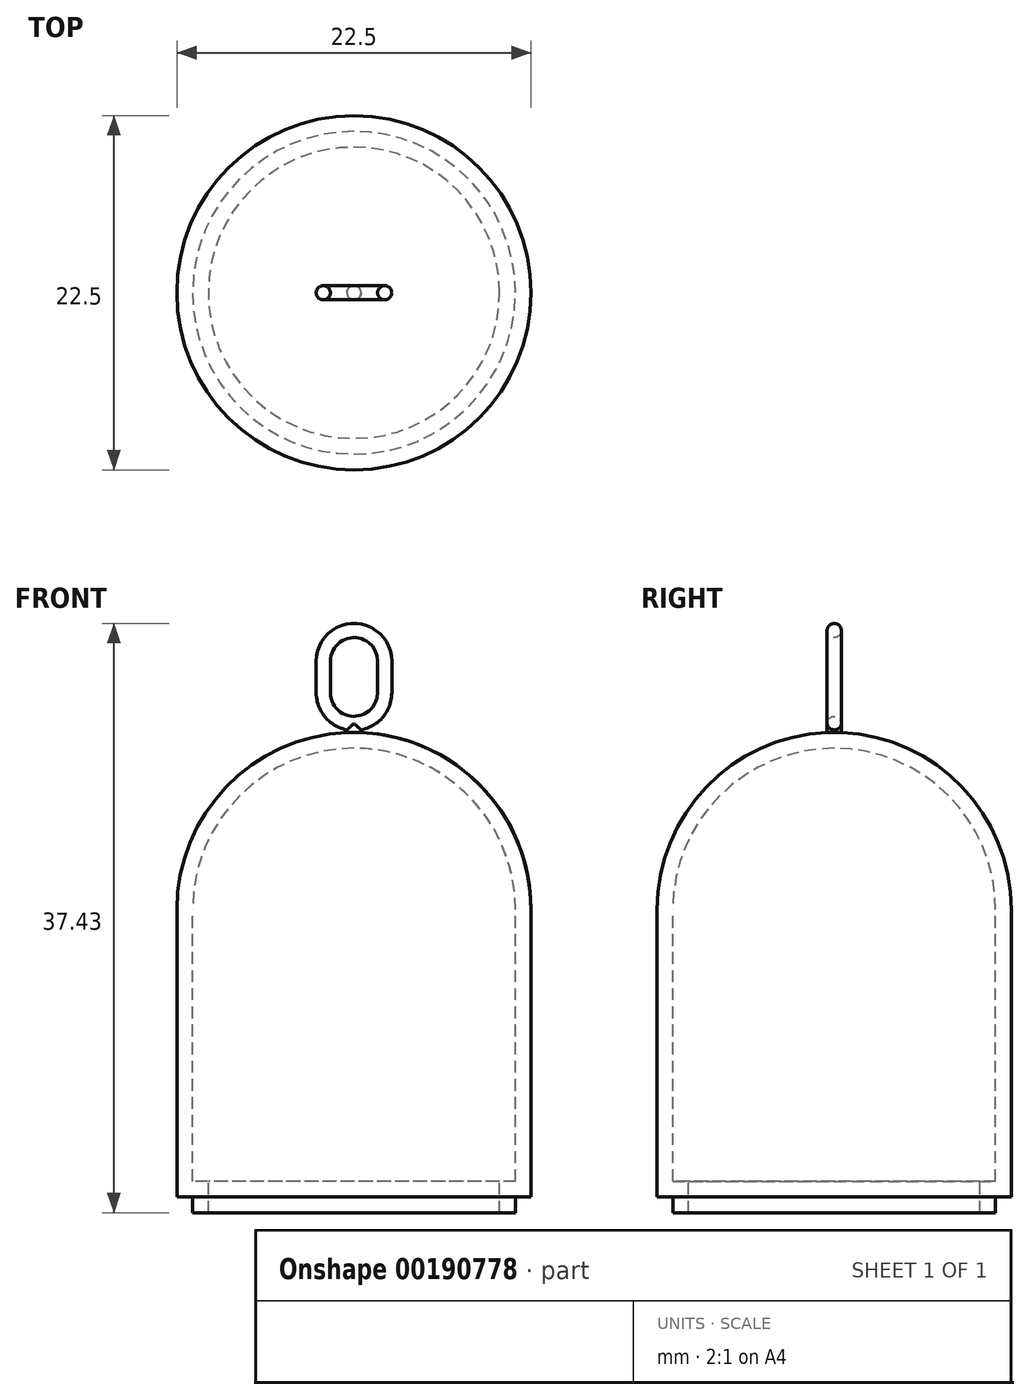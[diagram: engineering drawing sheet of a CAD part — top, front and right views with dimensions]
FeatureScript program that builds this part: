
annotation { "Feature Type Name" : "Feature", "Feature Type Description" : "" }
export const myFeature = defineFeature(function(context is Context, id is Id, definition is map)
    precondition{}
    {
        {
            var Q0;
            Q0=qCreatedBy(makeId("Front.planeOp"),FACE);
            var sketch = newSketch(context, id + "F0", { "sketchPlane" : qUnion([Q0])});
            skLineSegment(sketch, "E0.left", {"start": v(11.25, 18.75) * mm, "end": v(11.25, 0) * mm});
            skPoint(sketch, "E0.middle", {"position": v(0, 0) * mm});
            skPoint(sketch, "E1.visualSharp", {"position": v(11.25, 30) * mm});
            skArc(sketch, "E1.filletArc", {"start": v(11.25, 18.75) * mm, "mid": v(7.95, 26.7) * mm, "end": v(0, 30) * mm});
            skPoint(sketch, "E2", {"position": v(11.25, 0) * mm});
            skPoint(sketch, "E3", {"position": v(0, 30) * mm});
            skPoint(sketch, "E0.right.start.orphan", {"position": v(-11.25, 30) * mm});
            skPoint(sketch, "E0.top.end.orphan", {"position": v(-11.25, -30) * mm});
            skPoint(sketch, "E4.orphan", {"position": v(11.25, -30) * mm});
            skPoint(sketch, "E5", {"position": v(11.25, 0.5) * mm});
            skLineSegment(sketch, "E6", {"start": v(11.25, 0.5) * mm, "end": v(10.25, 0.5) * mm});
            skLineSegment(sketch, "E7", {"start": v(10.25, 0.5) * mm, "end": v(10.25, 0) * mm});
            skLineSegment(sketch, "E8", {"start": v(10.25, 0) * mm, "end": v(10.25, -0.5) * mm});
            skArc(sketch, "E9.0", {"start": v(10.25, 18.75) * mm, "mid": v(7.25, 26) * mm, "end": v(0, 29) * mm});
            skLineSegment(sketch, "E9.1", {"start": v(10.25, 18.75) * mm, "end": v(10.25, 1.5) * mm});
            skPoint(sketch, "E10", {"position": v(11.25, 1.5) * mm});
            skLineSegment(sketch, "E11", {"start": v(10.25, 1.5) * mm, "end": v(9.25, 1.5) * mm});
            skLineSegment(sketch, "E12", {"start": v(9.25, 1.5) * mm, "end": v(9.25, -0.5) * mm});
            skLineSegment(sketch, "E13", {"start": v(9.25, -0.5) * mm, "end": v(10.25, -0.5) * mm});
            skLineSegment(sketch, "E14", {"start": v(0, 30) * mm, "end": v(0, 29) * mm});
            skLineSegment(sketch, "E15.bottom", {"start": v(0, 31.03) * mm, "end": v(0, 31.03) * mm});
            skLineSegment(sketch, "E15.top", {"start": v(0, 36.03) * mm, "end": v(0, 36.03) * mm});
            skLineSegment(sketch, "E15.left", {"start": v(1.5, 32.53) * mm, "end": v(1.5, 34.53) * mm});
            skLineSegment(sketch, "E15.right", {"start": v(-1.5, 32.53) * mm, "end": v(-1.5, 34.53) * mm});
            skPoint(sketch, "E15.middle", {"position": v(0, 33.53) * mm});
            skLineSegment(sketch, "E16", {"start": v(-11.25, 30) * mm, "end": v(11.25, 30) * mm, "construction": true});
            skLineSegment(sketch, "E17", {"start": v(11.25, -30) * mm, "end": v(-11.25, -30) * mm, "construction": true});
            skLineSegment(sketch, "E18", {"start": v(-11.25, 30) * mm, "end": v(-11.25, -30) * mm, "construction": true});
            skLineSegment(sketch, "E19", {"start": v(11.25, 30) * mm, "end": v(11.25, -30) * mm, "construction": true});
            skPoint(sketch, "E20.visualSharp", {"position": v(1.5, 36.03) * mm});
            skArc(sketch, "E20.filletArc", {"start": v(1.5, 34.53) * mm, "mid": v(1.06, 35.6) * mm, "end": v(0, 36.03) * mm});
            skPoint(sketch, "E21.visualSharp", {"position": v(1.5, 31.03) * mm});
            skArc(sketch, "E21.filletArc", {"start": v(0, 31.03) * mm, "mid": v(1.06, 31.47) * mm, "end": v(1.5, 32.53) * mm});
            skPoint(sketch, "E22.visualSharp", {"position": v(-1.5, 31.03) * mm});
            skArc(sketch, "E22.filletArc", {"start": v(-1.5, 32.53) * mm, "mid": v(-1.06, 31.47) * mm, "end": v(0, 31.03) * mm});
            skPoint(sketch, "E23.visualSharp", {"position": v(-1.5, 36.03) * mm});
            skArc(sketch, "E23.filletArc", {"start": v(0, 36.03) * mm, "mid": v(-1.06, 35.6) * mm, "end": v(-1.5, 34.53) * mm});
            skLineSegment(sketch, "E24.0", {"start": v(2.4, 32.53) * mm, "end": v(2.4, 34.53) * mm});
            skArc(sketch, "E24.1", {"start": v(0, 36.93) * mm, "mid": v(-1.7, 36.23) * mm, "end": v(-2.4, 34.53) * mm});
            skLineSegment(sketch, "E24.2", {"start": v(-2.4, 32.53) * mm, "end": v(-2.4, 34.53) * mm});
            skArc(sketch, "E24.3", {"start": v(2.4, 34.53) * mm, "mid": v(1.7, 36.23) * mm, "end": v(0, 36.93) * mm});
            skArc(sketch, "E24.4", {"start": v(-2.4, 32.53) * mm, "mid": v(-1.7, 30.83) * mm, "end": v(0, 30.13) * mm});
            skArc(sketch, "E24.5", {"start": v(0, 30.13) * mm, "mid": v(1.7, 30.83) * mm, "end": v(2.4, 32.53) * mm});
            skLineSegment(sketch, "E25", {"start": v(0, 33.53) * mm, "end": v(2.4, 33.53) * mm, "construction": true});
            skLineSegment(sketch, "E26", {"start": v(0, 33.53) * mm, "end": v(-2.4, 33.53) * mm, "construction": true});
            skLineSegment(sketch, "E27.bottom", {"start": v(0.45, 30.3) * mm, "end": v(-0.45, 30.3) * mm});
            skLineSegment(sketch, "E27.top", {"start": v(0.45, 29.8) * mm, "end": v(-0.45, 29.8) * mm});
            skLineSegment(sketch, "E27.left", {"start": v(0.45, 30.3) * mm, "end": v(0.45, 29.8) * mm});
            skLineSegment(sketch, "E27.right", {"start": v(-0.45, 30.3) * mm, "end": v(-0.45, 29.8) * mm});
            skPoint(sketch, "E27.middle", {"position": v(0, 30.06) * mm});
            skLineSegment(sketch, "E28", {"start": v(10.25, 6.5) * mm, "end": v(-11.25, 6.5) * mm, "construction": true});
            skLineSegment(sketch, "E29", {"start": v(8.25, 6.5) * mm, "end": v(8.25, 3.5) * mm});
            skLineSegment(sketch, "E30", {"start": v(8.25, 3.5) * mm, "end": v(6.25, 3.5) * mm});
            skLineSegment(sketch, "E31", {"start": v(6.25, 3.5) * mm, "end": v(6.25, -0.5) * mm});
            skLineSegment(sketch, "E32", {"start": v(6.25, -0.5) * mm, "end": v(11.25, -0.5) * mm});
            skSolve(sketch);
        }
        {
            var Q0;
            Q0=qCreatedBy(makeId("Top.planeOp"),FACE);
            var sketch = newSketch(context, id + "F1", { "sketchPlane" : qUnion([Q0])});
            skCircle(sketch, "E33", {"center": v(0, 0) * mm, "radius": 11.25 * mm});
            skSolve(sketch);
        }
        {
            var Q0;
            {var subQ0=sQuery(id+"F0.wireOp",EDGE,"E14");var subQ1=sQuery(id+"F0.wireOp",EDGE,"E1.filletArc");var subQ2=makeQuery(id+"F0.imprint","INTERSECT",VERTEX,{"derivedFrom":[subQ1,subQ0]});Q0=makeQuery(id+"F0.imprint","IMPRINT",FACE,{"disambiguationData":[TD([[makeQuery(id+"F0.imprint","IMPRINT",EDGE,{"disambiguationData":[TD([[subQ2,1.0]])],"derivedFrom":subQ1}),1.0]])]});}
            var Q1;
            {var subQ7=sQuery(id+"F0.wireOp",EDGE,"E6");Q1=makeQuery(id+"F0.imprint","IMPRINT",FACE,{"disambiguationData":[TD([[makeQuery(id+"F0.imprint","IMPRINT",EDGE,{"derivedFrom":subQ7}),-1.0]])]});}
            var Q2;
            Q2=sQuery(id+"F1.wireOp",EDGE,"E33");
            sweep(context, id + "F2", {"profiles" : qUnion([Q0, Q1]), "path" : qUnion([Q2])});
        }
        {
            var Q0;
            {var subQ0=sQuery(id+"F0.wireOp",EDGE,"E14");var subQ1=sQuery(id+"F0.wireOp",EDGE,"E1.filletArc");var subQ2=makeQuery(id+"F0.imprint","INTERSECT",VERTEX,{"derivedFrom":[subQ1,subQ0]});Q0=makeQuery(id+"F0.imprint","IMPRINT",FACE,{"disambiguationData":[TD([[makeQuery(id+"F0.imprint","IMPRINT",EDGE,{"disambiguationData":[TD([[subQ2,1.0]])],"derivedFrom":subQ1}),1.0]])]});}
            var Q1;
            Q1=makeQuery(id+"F0.imprint","IMPRINT",FACE,{"disambiguationData":[TD([[makeQuery(id+"F0.imprint","IMPRINT",EDGE,{"derivedFrom":sQuery(id+"F0.wireOp",EDGE,"E15.left")}),-1.0]])]});
            var Q2;
            {var subQ1=sQuery(id+"F0.wireOp",EDGE,"E27.bottom");Q2=makeQuery(id+"F0.imprint","IMPRINT",FACE,{"disambiguationData":[TD([[makeQuery(id+"F0.imprint","IMPRINT",EDGE,{"derivedFrom":subQ1}),1.0]])]});}
            var Q3;
            {var subQ7=sQuery(id+"F0.wireOp",EDGE,"E1.filletArc");var subQ9=sQuery(id+"F0.wireOp",EDGE,"E14");var subQ10=makeQuery(id+"F0.imprint","INTERSECT",VERTEX,{"derivedFrom":[subQ7,subQ9]});Q3=makeQuery(id+"F0.imprint","IMPRINT",FACE,{"disambiguationData":[TD([[makeQuery(id+"F0.imprint","IMPRINT",EDGE,{"disambiguationData":[TD([[subQ10,1.0]])],"derivedFrom":subQ7}),-1.0]])]});}
            extrude(context, id + "F3", {"entities" : qUnion([Q0, Q1, Q2, Q3]), "operationType" : NewBodyOperationType.ADD, "depth" : .45 * mm, "hasSecondDirection" : true, "secondDirectionOppositeDirection" : true, "secondDirectionDepth" : .45 * mm});
        }
        {
            var Q0;
            Q0=makeQuery(id+"F3.opExtrude","CAP_EDGE",EDGE,{"disambiguationData":[OSD([sQuery(id+"F0.wireOp",EDGE,"E21.filletArc"),sQuery(id+"F0.wireOp",EDGE,"E22.filletArc")])],"isStart":false});
            var Q1;
            Q1=makeQuery(id+"F3.opExtrude","CAP_EDGE",EDGE,{"disambiguationData":[OSD([sQuery(id+"F0.wireOp",EDGE,"E21.filletArc"),sQuery(id+"F0.wireOp",EDGE,"E22.filletArc")])],"isStart":true});
            var Q2;
            Q2=makeQuery(id+"F3.opExtrude","CAP_EDGE",EDGE,{"disambiguationData":[OSD([sQuery(id+"F0.wireOp",EDGE,"E24.1"),sQuery(id+"F0.wireOp",EDGE,"E24.3")])],"isStart":false});
            var Q3;
            Q3=makeQuery(id+"F3.opExtrude","CAP_EDGE",EDGE,{"disambiguationData":[OSD([sQuery(id+"F0.wireOp",EDGE,"E24.1"),sQuery(id+"F0.wireOp",EDGE,"E24.3")])],"isStart":true});
            var Q4;
            Q4=makeQuery(id+"F3.opExtrude","CAP_EDGE",EDGE,{"disambiguationData":[OSD([sQuery(id+"F0.wireOp",EDGE,"E27.left")])],"isStart":false});
            var Q5;
            Q5=makeQuery(id+"F3.opExtrude","CAP_EDGE",EDGE,{"disambiguationData":[OSD([sQuery(id+"F0.wireOp",EDGE,"E27.left")])],"isStart":true});
            var Q6;
            Q6=makeQuery(id+"F3.opExtrude","CAP_EDGE",EDGE,{"disambiguationData":[OSD([sQuery(id+"F0.wireOp",EDGE,"E27.right")])],"isStart":false});
            var Q7;
            Q7=makeQuery(id+"F3.opExtrude","CAP_EDGE",EDGE,{"disambiguationData":[OSD([sQuery(id+"F0.wireOp",EDGE,"E27.right")])],"isStart":true});
            fillet(context, id + "F4", {"entities" : qUnion([Q0, Q1, Q2, Q3, Q4, Q5, Q6, Q7]), "radius" : .45 * mm, "tangentPropagation" : true, "allowEdgeOverflow" : false});
        }
    });
